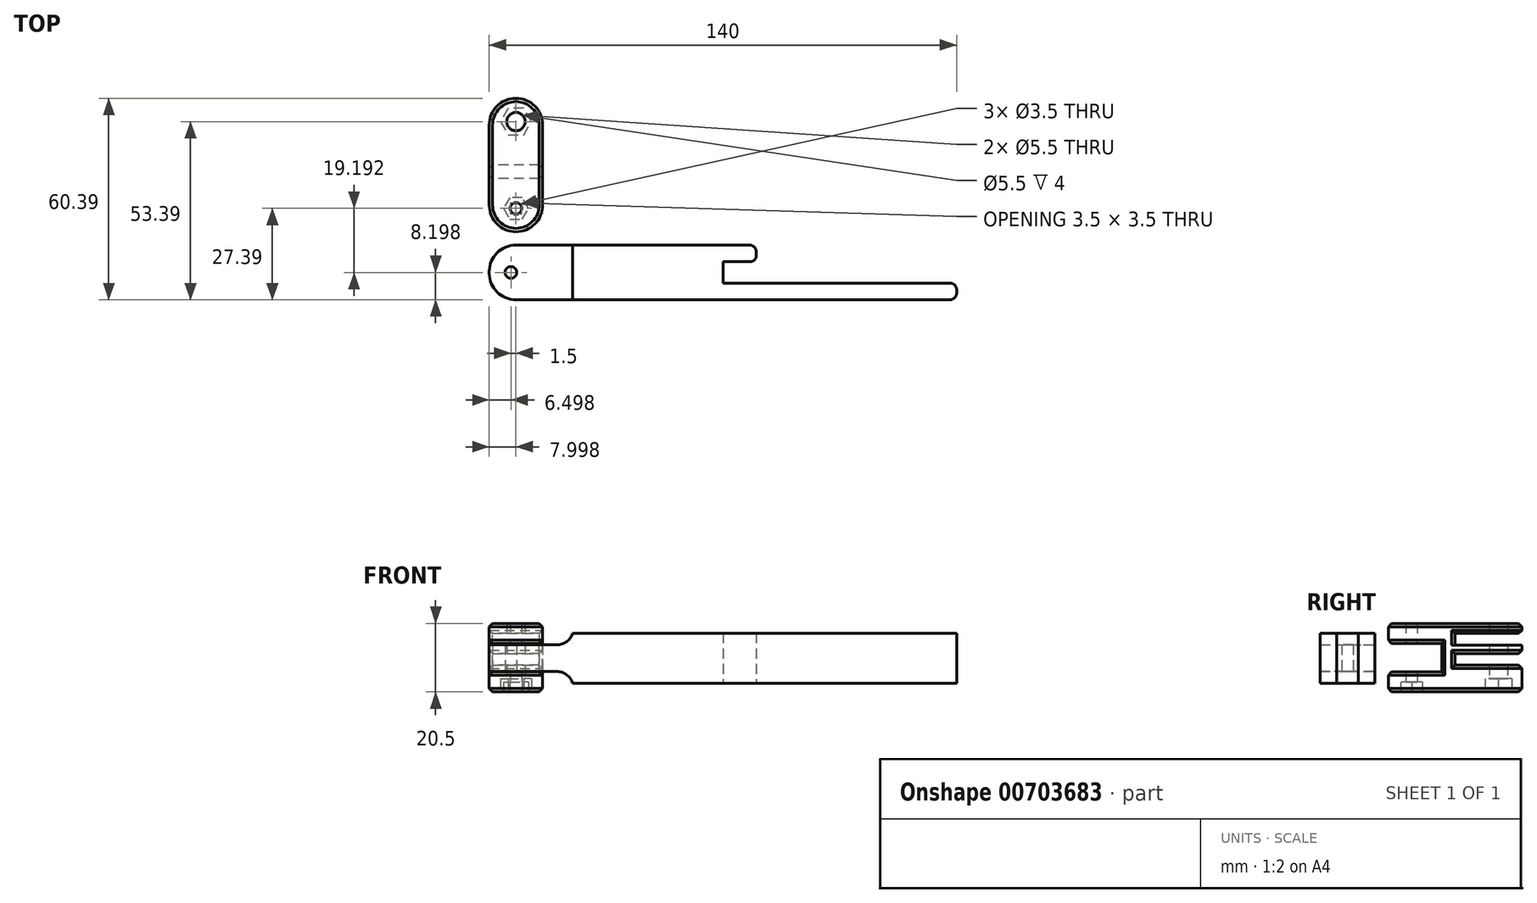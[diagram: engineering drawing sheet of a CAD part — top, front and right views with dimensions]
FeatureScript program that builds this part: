
annotation { "Feature Type Name" : "Feature", "Feature Type Description" : "" }
export const myFeature = defineFeature(function(context is Context, id is Id, definition is map)
    precondition{}
    {
        {
            var Q0;
            Q0=qCreatedBy(makeId("Top.planeOp"),FACE);
            var sketch = newSketch(context, id + "F0", { "sketchPlane" : qUnion([Q0])});
            skLineSegment(sketch, "E0.bottom", {"start": v(-2.1, -4) * mm, "end": v(7.9, -4) * mm});
            skLineSegment(sketch, "E1.top", {"start": v(7.9, 1) * mm, "end": v(-2.1, 1) * mm});
            skLineSegment(sketch, "E1.left", {"start": v(7.9, -4) * mm, "end": v(7.9, 1) * mm});
            skLineSegment(sketch, "E2.bottom", {"start": v(-2.1, -10.4) * mm, "end": v(67.9, -10.4) * mm});
            skLineSegment(sketch, "E2.top", {"start": v(-2.1, -15.4) * mm, "end": v(67.9, -15.4) * mm});
            skLineSegment(sketch, "E2.right", {"start": v(67.9, -10.4) * mm, "end": v(67.9, -15.4) * mm});
            skLineSegment(sketch, "E3.bottom", {"start": v(-2.1, 1) * mm, "end": v(-2.1, 1) * mm});
            skLineSegment(sketch, "E3.top", {"start": v(-2.1, -15.4) * mm, "end": v(-2.1, -15.4) * mm});
            skLineSegment(sketch, "E3.left", {"start": v(-2.1, -4) * mm, "end": v(-2.1, -10.4) * mm});
            skLineSegment(sketch, "E3.right", {"start": v(-2.1, -4) * mm, "end": v(-2.1, -10.4) * mm});
            skLineSegment(sketch, "E4.bottom", {"start": v(-2.1, 1) * mm, "end": v(-72.1, 1) * mm});
            skLineSegment(sketch, "E4.top", {"start": v(-2.1, -15.4) * mm, "end": v(-72.1, -15.4) * mm});
            skLineSegment(sketch, "E4.right", {"start": v(-72.1, 1) * mm, "end": v(-72.1, -15.4) * mm});
            skPoint(sketch, "E5.orphan", {"position": v(0, -4) * mm});
            skPoint(sketch, "E0.top.end.orphan", {"position": v(15, 0) * mm});
            skPoint(sketch, "E0.top.start.orphan", {"position": v(0, -10.4) * mm});
            skSolve(sketch);
        }
        {
            var Q0;
            Q0=makeQuery(id+"F0.imprint","IMPRINT",FACE,{"disambiguationData":[TD([[makeQuery(id+"F0.imprint","IMPRINT",EDGE,{"derivedFrom":sQuery(id+"F0.wireOp",EDGE,"E0.bottom")}),1.0]])]});
            extrude(context, id + "F1", {"entities" : qUnion([Q0]), "depth" : 15 * mm, "offsetDistance" : 25 * mm});
        }
        {
            var Q0;
            Q0=makeQuery(id+"F1.opExtrude","SWEPT_FACE",FACE,{"disambiguationData":[OSD([sQuery(id+"F0.wireOp",EDGE,"E4.right")])]});
            var sketch = newSketch(context, id + "F2", { "sketchPlane" : qUnion([Q0])});
            skLineSegment(sketch, "E6.top", {"start": v(-5, -2.6) * mm, "end": v(-5, 17.9) * mm});
            skLineSegment(sketch, "E7.top", {"start": v(-45, 8.9) * mm, "end": v(-45, 11.4) * mm});
            skLineSegment(sketch, "E8.top", {"start": v(-25, 11.4) * mm, "end": v(-25, 11.4) * mm});
            skLineSegment(sketch, "E8.left", {"start": v(-45, 11.4) * mm, "end": v(-25, 11.4) * mm});
            skLineSegment(sketch, "E8.right", {"start": v(-45, 14.9) * mm, "end": v(-25, 14.9) * mm});
            skLineSegment(sketch, "E9.bottom", {"start": v(-45, 14.9) * mm, "end": v(-45, 17.9) * mm});
            skLineSegment(sketch, "E10.left", {"start": v(-45, 17.9) * mm, "end": v(-25, 17.9) * mm});
            skLineSegment(sketch, "E11.top", {"start": v(-25, 5.4) * mm, "end": v(-25, 5.4) * mm});
            skLineSegment(sketch, "E11.left", {"start": v(-45, 8.9) * mm, "end": v(-25, 8.9) * mm});
            skLineSegment(sketch, "E11.right", {"start": v(-45, 5.4) * mm, "end": v(-25, 5.4) * mm});
            skLineSegment(sketch, "E12.bottom", {"start": v(-45, 5.4) * mm, "end": v(-45, -2.6) * mm});
            skLineSegment(sketch, "E13.left", {"start": v(-45, -2.6) * mm, "end": v(-25.08, -2.6) * mm});
            skLineSegment(sketch, "E14", {"start": v(-25.08, -2.6) * mm, "end": v(-5, -2.6) * mm});
            skLineSegment(sketch, "E15", {"start": v(-25, 17.9) * mm, "end": v(-5, 17.9) * mm});
            skPoint(sketch, "E6.left.end.orphan", {"position": v(-1, -14.6) * mm});
            skPoint(sketch, "E13.top.end.orphan", {"position": v(-25, -10.68) * mm});
            skPoint(sketch, "E10.top.end.orphan", {"position": v(-25, 29.32) * mm});
            skLineSegment(sketch, "E16.bottom", {"start": v(-5, 3.4) * mm, "end": v(-21, 3.4) * mm});
            skLineSegment(sketch, "E16.top", {"start": v(-5, 11.9) * mm, "end": v(-21, 11.9) * mm});
            skLineSegment(sketch, "E16.left", {"start": v(-5, 3.4) * mm, "end": v(-5, 11.9) * mm});
            skLineSegment(sketch, "E16.right", {"start": v(-21, 3.4) * mm, "end": v(-21, 11.9) * mm});
            skLineSegment(sketch, "E17", {"start": v(-25, 14.9) * mm, "end": v(-25, 11.4) * mm});
            skLineSegment(sketch, "E18", {"start": v(-25, 8.9) * mm, "end": v(-25, 5.4) * mm});
            skSolve(sketch);
        }
        {
            var Q0;
            Q0=makeQuery(id+"F2.imprint","IMPRINT",FACE,{"disambiguationData":[TD([[makeQuery(id+"F2.imprint","IMPRINT",EDGE,{"derivedFrom":sQuery(id+"F2.wireOp",EDGE,"E12.bottom")}),1.0]])]});
            var Q1;
            {var subQ0=sQuery(id+"F2.wireOp",EDGE,"E7.bottom");Q1=makeQuery(id+"F2.imprint","IMPRINT",FACE,{"disambiguationData":[TD([[makeQuery(id+"F2.imprint","IMPRINT",EDGE,{"derivedFrom":subQ0}),1.0]])]});}
            var Q2;
            Q2=makeQuery(id+"F2.imprint","IMPRINT",FACE,{"disambiguationData":[TD([[makeQuery(id+"F2.imprint","IMPRINT",EDGE,{"derivedFrom":sQuery(id+"F2.wireOp",EDGE,"E9.bottom")}),-1.0]])]});
            var Q3;
            {var subQ1=sQuery(id+"F2.wireOp",EDGE,"E7.bottom");Q3=makeQuery(id+"F2.imprint","IMPRINT",FACE,{"disambiguationData":[TD([[makeQuery(id+"F2.imprint","IMPRINT",EDGE,{"derivedFrom":subQ1}),-1.0]])]});}
            extrude(context, id + "F3", {"entities" : qUnion([Q0, Q1, Q2, Q3]), "operationType" : NewBodyOperationType.ADD, "oppositeDirection" : true, "depth" : 16 * mm, "offsetDistance" : 25 * mm});
        }
        {
            var Q0;
            Q0=makeQuery(id+"F3.opExtrude","SWEPT_FACE",FACE,{"disambiguationData":[OSD([sQuery(id+"F2.wireOp",EDGE,"E13.left"),sQuery(id+"F2.wireOp",EDGE,"E14")])]});
            var sketch = newSketch(context, id + "F4", { "sketchPlane" : qUnion([Q0])});
            skCircle(sketch, "E19", {"center": v(-64.1, -38) * mm, "radius": 2.75 * mm});
            skPoint(sketch, "E19.centerSnap0", {"position": v(-64.1, -45) * mm});
            skCircle(sketch, "E20", {"center": v(-64.1, -12) * mm, "radius": 1.75 * mm});
            skSolve(sketch);
        }
        {
            var Q0;
            Q0=makeQuery(id+"F3.opExtrude","CAP_EDGE",EDGE,{"disambiguationData":[OSD([sQuery(id+"F2.wireOp",EDGE,"E12.bottom")])],"isStart":false});
            var Q1;
            Q1=makeQuery(id+"F3.opExtrude","CAP_EDGE",EDGE,{"disambiguationData":[OSD([sQuery(id+"F2.wireOp",EDGE,"E7.top")])],"isStart":false});
            var Q2;
            Q2=makeQuery(id+"F3.opExtrude","CAP_EDGE",EDGE,{"disambiguationData":[OSD([sQuery(id+"F2.wireOp",EDGE,"E9.bottom")])],"isStart":false});
            var Q3;
            Q3=makeQuery(id+"F3.opExtrude","CAP_EDGE",EDGE,{"disambiguationData":[OSD([sQuery(id+"F2.wireOp",EDGE,"E12.bottom")])],"isStart":true});
            var Q4;
            Q4=makeQuery(id+"F3.opExtrude","CAP_EDGE",EDGE,{"disambiguationData":[OSD([sQuery(id+"F2.wireOp",EDGE,"E7.top")])],"isStart":true});
            var Q5;
            Q5=makeQuery(id+"F3.opExtrude","CAP_EDGE",EDGE,{"disambiguationData":[OSD([sQuery(id+"F2.wireOp",EDGE,"E9.bottom")])],"isStart":true});
            var Q6;
            Q6=makeQuery(id+"F3.opExtrude","CAP_EDGE",EDGE,{"disambiguationData":[OSD([sQuery(id+"F2.wireOp",EDGE,"E6.top")])],"isStart":true});
            var Q7;
            Q7=makeQuery(id+"F3.opExtrude","CAP_EDGE",EDGE,{"disambiguationData":[OSD([sQuery(id+"F2.wireOp",EDGE,"E6.top")])],"isStart":false});
            fillet(context, id + "F5", {"entities" : qUnion([Q0, Q1, Q2, Q3, Q4, Q5, Q6, Q7]), "radius" : 8 * mm, "tangentPropagation" : true, "allowEdgeOverflow" : false});
        }
        {
            var Q0;
            Q0=makeQuery(id+"F4.imprint","IMPRINT",FACE,{"disambiguationData":[TD([[makeQuery(id+"F4.imprint","IMPRINT",EDGE,{"derivedFrom":sQuery(id+"F4.wireOp",EDGE,"E19")}),1.0]])]});
            var Q1;
            Q1=makeQuery(id+"F4.imprint","IMPRINT",FACE,{"disambiguationData":[TD([[makeQuery(id+"F4.imprint","IMPRINT",EDGE,{"derivedFrom":sQuery(id+"F4.wireOp",EDGE,"E20")}),1.0]])]});
            extrude(context, id + "F6", {"entities" : qUnion([Q0, Q1]), "operationType" : NewBodyOperationType.REMOVE, "oppositeDirection" : true, "depth" : 25 * mm, "offsetDistance" : 25 * mm});
        }
        {
            var Q0;
            Q0=makeQuery(id+"F3.opExtrude","SWEPT_FACE",FACE,{"disambiguationData":[OSD([sQuery(id+"F2.wireOp",EDGE,"E13.left"),sQuery(id+"F2.wireOp",EDGE,"E14")])]});
            var sketch = newSketch(context, id + "F7", { "sketchPlane" : qUnion([Q0])});
            skCircle(sketch, "E21.cCircle", {"center": v(-64.1, -38) * mm, "radius": 4 * mm, "construction": true});
            skLineSegment(sketch, "E21.0", {"start": v(-66.4, -34) * mm, "end": v(-61.78, -34) * mm});
            skLineSegment(sketch, "E21.1", {"start": v(-61.78, -34) * mm, "end": v(-59.47, -38) * mm});
            skLineSegment(sketch, "E21.2", {"start": v(-59.47, -38) * mm, "end": v(-61.78, -42) * mm});
            skLineSegment(sketch, "E21.3", {"start": v(-61.78, -42) * mm, "end": v(-66.4, -42) * mm});
            skLineSegment(sketch, "E21.4", {"start": v(-66.4, -42) * mm, "end": v(-68.71, -38) * mm});
            skLineSegment(sketch, "E21.5", {"start": v(-68.71, -38) * mm, "end": v(-66.4, -34) * mm});
            skPoint(sketch, "E21.0.midPoint", {"position": v(-64.1, -34) * mm});
            skSolve(sketch);
        }
        {
            var Q0;
            Q0=makeQuery(id+"F7.imprint","IMPRINT",FACE,{"disambiguationData":[TD([[makeQuery(id+"F7.imprint","IMPRINT",EDGE,{"derivedFrom":sQuery(id+"F7.wireOp",EDGE,"E21.0")}),-1.0]])]});
            extrude(context, id + "F8", {"entities" : qUnion([Q0]), "operationType" : NewBodyOperationType.REMOVE, "oppositeDirection" : true, "depth" : 4 * mm, "offsetDistance" : 25 * mm});
        }
        {
            var Q0;
            Q0=makeQuery(id+"F1.opExtrude","SWEPT_EDGE",EDGE,{"disambiguationData":[OSD([sQuery(id+"F0.wireOp",EDGE,"E1.top"),sQuery(id+"F0.wireOp",EDGE,"E1.left")])]});
            var Q1;
            Q1=makeQuery(id+"F1.opExtrude","SWEPT_EDGE",EDGE,{"disambiguationData":[OSD([sQuery(id+"F0.wireOp",EDGE,"E2.bottom"),sQuery(id+"F0.wireOp",EDGE,"E2.right")])]});
            var Q2;
            Q2=makeQuery(id+"F1.opExtrude","SWEPT_EDGE",EDGE,{"disambiguationData":[OSD([sQuery(id+"F0.wireOp",EDGE,"E2.top"),sQuery(id+"F0.wireOp",EDGE,"E2.right")])]});
            var Q3;
            Q3=makeQuery(id+"F1.opExtrude","SWEPT_EDGE",EDGE,{"disambiguationData":[OSD([sQuery(id+"F0.wireOp",EDGE,"E0.bottom"),sQuery(id+"F0.wireOp",EDGE,"E1.left")])]});
            fillet(context, id + "F9", {"entities" : qUnion([Q0, Q1, Q2, Q3]), "radius" : 2 * mm, "tangentPropagation" : true, "allowEdgeOverflow" : false});
        }
        {
            var Q0;
            Q0=makeQuery(id+"F1.opExtrude","SWEPT_FACE",FACE,{"disambiguationData":[OSD([sQuery(id+"F0.wireOp",EDGE,"E4.right")])]});
            var sketch = newSketch(context, id + "F10", { "sketchPlane" : qUnion([Q0])});
            skLineSegment(sketch, "E22.bottom", {"start": v(-1, 0) * mm, "end": v(15.4, 0) * mm});
            skLineSegment(sketch, "E22.top", {"start": v(-1, 3.5) * mm, "end": v(15.4, 3.5) * mm});
            skLineSegment(sketch, "E22.left", {"start": v(-1, 0) * mm, "end": v(-1, 3.5) * mm});
            skLineSegment(sketch, "E22.right", {"start": v(15.4, 0) * mm, "end": v(15.4, 3.5) * mm});
            skLineSegment(sketch, "E23.bottom", {"start": v(-1, 15) * mm, "end": v(15.4, 15) * mm});
            skLineSegment(sketch, "E23.top", {"start": v(-1, 11.5) * mm, "end": v(15.4, 11.5) * mm});
            skLineSegment(sketch, "E23.left", {"start": v(-1, 15) * mm, "end": v(-1, 11.5) * mm});
            skLineSegment(sketch, "E23.right", {"start": v(15.4, 15) * mm, "end": v(15.4, 11.5) * mm});
            skSolve(sketch);
        }
        {
            var Q0;
            Q0=makeQuery(id+"F10.imprint","IMPRINT",FACE,{"disambiguationData":[TD([[makeQuery(id+"F10.imprint","IMPRINT",EDGE,{"derivedFrom":sQuery(id+"F10.wireOp",EDGE,"E22.bottom")}),1.0]])]});
            var Q1;
            Q1=makeQuery(id+"F10.imprint","IMPRINT",FACE,{"disambiguationData":[TD([[makeQuery(id+"F10.imprint","IMPRINT",EDGE,{"derivedFrom":sQuery(id+"F10.wireOp",EDGE,"E23.bottom")}),-1.0]])]});
            extrude(context, id + "F11", {"entities" : qUnion([Q0, Q1]), "operationType" : NewBodyOperationType.REMOVE, "oppositeDirection" : true, "depth" : 25 * mm, "offsetDistance" : 25 * mm});
        }
        {
            var Q0;
            Q0=makeQuery(id+"F1.opExtrude","SWEPT_EDGE",EDGE,{"disambiguationData":[OSD([sQuery(id+"F0.wireOp",EDGE,"E4.bottom"),sQuery(id+"F0.wireOp",EDGE,"E4.right")])]});
            var Q1;
            Q1=makeQuery(id+"F1.opExtrude","SWEPT_EDGE",EDGE,{"disambiguationData":[OSD([sQuery(id+"F0.wireOp",EDGE,"E4.top"),sQuery(id+"F0.wireOp",EDGE,"E4.right")])]});
            fillet(context, id + "F12", {"entities" : qUnion([Q0, Q1]), "radius" : 8 * mm, "tangentPropagation" : true, "defaultsChanged" : true, "vertexSettings" : [], "allowEdgeOverflow" : false});
        }
        {
            var Q0;
            Q0=makeQuery(id+"F11.boolean.opBoolean","COPY",FACE,{"derivedFrom":makeQuery(id+"F11.opExtrude","SWEPT_FACE",FACE,{"disambiguationData":[OSD([sQuery(id+"F10.wireOp",EDGE,"E22.top")])]})});
            var sketch = newSketch(context, id + "F13", { "sketchPlane" : qUnion([Q0])});
            skCircle(sketch, "E24", {"center": v(-65.6, 7.2) * mm, "radius": 1.75 * mm});
            skPoint(sketch, "E24.centerSnap0", {"position": v(-72.1, 7.2) * mm});
            skSolve(sketch);
        }
        {
            var Q0;
            Q0=makeQuery(id+"F13.imprint","IMPRINT",FACE,{"disambiguationData":[TD([[makeQuery(id+"F13.imprint","IMPRINT",EDGE,{"derivedFrom":sQuery(id+"F13.wireOp",EDGE,"E24")}),1.0]])]});
            extrude(context, id + "F14", {"entities" : qUnion([Q0]), "operationType" : NewBodyOperationType.REMOVE, "oppositeDirection" : true, "depth" : 25 * mm, "offsetDistance" : 25 * mm});
        }
        {
            var Q0;
            Q0=makeQuery(id+"F11.boolean.opBoolean","COPY",EDGE,{"derivedFrom":makeQuery(id+"F11.opExtrude","CAP_EDGE",EDGE,{"disambiguationData":[OSD([sQuery(id+"F10.wireOp",EDGE,"E22.top")])],"isStart":false})});
            var Q1;
            Q1=makeQuery(id+"F11.boolean.opBoolean","COPY",EDGE,{"derivedFrom":makeQuery(id+"F11.opExtrude","CAP_EDGE",EDGE,{"disambiguationData":[OSD([sQuery(id+"F10.wireOp",EDGE,"E23.top")])],"isStart":false})});
            fillet(context, id + "F15", {"entities" : qUnion([Q0, Q1]), "radius" : 5 * mm, "tangentPropagation" : true, "allowEdgeOverflow" : false});
        }
        {
            var Q0;
            Q0=makeQuery(id+"F3.opExtrude","SWEPT_FACE",FACE,{"disambiguationData":[OSD([sQuery(id+"F2.wireOp",EDGE,"E13.left"),sQuery(id+"F2.wireOp",EDGE,"E14")])]});
            var sketch = newSketch(context, id + "F16", { "sketchPlane" : qUnion([Q0])});
            skCircle(sketch, "E25.cCircle", {"center": v(-64.1, -38) * mm, "radius": 3.75 * mm, "construction": true});
            skLineSegment(sketch, "E25.0", {"start": v(-66.26, -34.25) * mm, "end": v(-61.93, -34.25) * mm});
            skLineSegment(sketch, "E25.1", {"start": v(-61.93, -34.25) * mm, "end": v(-59.76, -38) * mm});
            skLineSegment(sketch, "E25.2", {"start": v(-59.76, -38) * mm, "end": v(-61.93, -41.75) * mm});
            skLineSegment(sketch, "E25.3", {"start": v(-61.93, -41.75) * mm, "end": v(-66.26, -41.75) * mm});
            skLineSegment(sketch, "E25.4", {"start": v(-66.26, -41.75) * mm, "end": v(-68.42, -38) * mm});
            skLineSegment(sketch, "E25.5", {"start": v(-68.42, -38) * mm, "end": v(-66.26, -34.25) * mm});
            skPoint(sketch, "E25.0.midPoint", {"position": v(-64.1, -34.25) * mm});
            skCircle(sketch, "E26.cCircle", {"center": v(-64.1, -12) * mm, "radius": 3.25 * mm, "construction": true});
            skLineSegment(sketch, "E26.0", {"start": v(-65.97, -8.75) * mm, "end": v(-62.22, -8.75) * mm});
            skLineSegment(sketch, "E26.1", {"start": v(-62.22, -8.75) * mm, "end": v(-60.34, -12) * mm});
            skLineSegment(sketch, "E26.2", {"start": v(-60.34, -12) * mm, "end": v(-62.22, -15.25) * mm});
            skLineSegment(sketch, "E26.3", {"start": v(-62.22, -15.25) * mm, "end": v(-65.97, -15.25) * mm});
            skLineSegment(sketch, "E26.4", {"start": v(-65.97, -15.25) * mm, "end": v(-67.84, -12) * mm});
            skLineSegment(sketch, "E26.5", {"start": v(-67.84, -12) * mm, "end": v(-65.97, -8.75) * mm});
            skPoint(sketch, "E26.0.midPoint", {"position": v(-64.1, -8.75) * mm});
            skSolve(sketch);
        }
        {
            var Q0;
            Q0=makeQuery(id+"F16.imprint","IMPRINT",FACE,{"disambiguationData":[TD([[makeQuery(id+"F16.imprint","IMPRINT",EDGE,{"derivedFrom":sQuery(id+"F16.wireOp",EDGE,"E25.0")}),-1.0]])]});
            var Q1;
            Q1=makeQuery(id+"F16.imprint","IMPRINT",FACE,{"disambiguationData":[TD([[makeQuery(id+"F16.imprint","IMPRINT",EDGE,{"derivedFrom":sQuery(id+"F16.wireOp",EDGE,"E26.0")}),-1.0]])]});
            extrude(context, id + "F17", {"entities" : qUnion([Q0, Q1]), "operationType" : NewBodyOperationType.REMOVE, "oppositeDirection" : true, "depth" : 3 * mm, "offsetDistance" : 25 * mm});
        }
        {
            var Q0;
            Q0=makeQuery(id+"F3.opExtrude","CAP_EDGE",EDGE,{"disambiguationData":[OSD([sQuery(id+"F2.wireOp",EDGE,"E10.left"),sQuery(id+"F2.wireOp",EDGE,"E15")])],"isStart":true});
            var Q1;
            Q1=makeQuery(id+"F3.opExtrude","CAP_EDGE",EDGE,{"disambiguationData":[OSD([sQuery(id+"F2.wireOp",EDGE,"E13.left"),sQuery(id+"F2.wireOp",EDGE,"E14")])],"isStart":true});
            var Q2;
            Q2=makeQuery(id+"F3.opExtrude","CAP_EDGE",EDGE,{"disambiguationData":[OSD([sQuery(id+"F2.wireOp",EDGE,"E11.right")])],"isStart":true});
            var Q3;
            Q3=makeQuery(id+"F3.opExtrude","CAP_EDGE",EDGE,{"disambiguationData":[OSD([sQuery(id+"F2.wireOp",EDGE,"E11.left")])],"isStart":true});
            var Q4;
            Q4=makeQuery(id+"F3.opExtrude","CAP_EDGE",EDGE,{"disambiguationData":[OSD([sQuery(id+"F2.wireOp",EDGE,"E8.right")])],"isStart":true});
            var Q5;
            Q5=makeQuery(id+"F3.opExtrude","CAP_EDGE",EDGE,{"disambiguationData":[OSD([sQuery(id+"F2.wireOp",EDGE,"E16.top")])],"isStart":true});
            var Q6;
            Q6=makeQuery(id+"F3.opExtrude","CAP_EDGE",EDGE,{"disambiguationData":[OSD([sQuery(id+"F2.wireOp",EDGE,"E16.right")])],"isStart":true});
            var Q7;
            Q7=makeQuery(id+"F3.opExtrude","CAP_EDGE",EDGE,{"disambiguationData":[OSD([sQuery(id+"F2.wireOp",EDGE,"E16.bottom")])],"isStart":true});
            var Q8;
            Q8=makeQuery(id+"F3.opExtrude","CAP_EDGE",EDGE,{"disambiguationData":[OSD([sQuery(id+"F2.wireOp",EDGE,"E16.right")])],"isStart":false});
            var Q9;
            Q9=makeQuery(id+"F3.opExtrude","CAP_EDGE",EDGE,{"disambiguationData":[OSD([sQuery(id+"F2.wireOp",EDGE,"E18")])],"isStart":false});
            var Q10;
            Q10=makeQuery(id+"F3.opExtrude","CAP_EDGE",EDGE,{"disambiguationData":[OSD([sQuery(id+"F2.wireOp",EDGE,"E17")])],"isStart":false});
            var Q11;
            Q11=makeQuery(id+"F3.opExtrude","CAP_EDGE",EDGE,{"disambiguationData":[OSD([sQuery(id+"F2.wireOp",EDGE,"E18")])],"isStart":true});
            var Q12;
            Q12=makeQuery(id+"F3.opExtrude","CAP_EDGE",EDGE,{"disambiguationData":[OSD([sQuery(id+"F2.wireOp",EDGE,"E17")])],"isStart":true});
            chamfer(context, id + "F18", {"entities" : qUnion([Q0, Q1, Q2, Q3, Q4, Q5, Q6, Q7, Q8, Q9, Q10, Q11, Q12]), "width" : 1 * mm, "tangentPropagation" : true});
        }
    });
